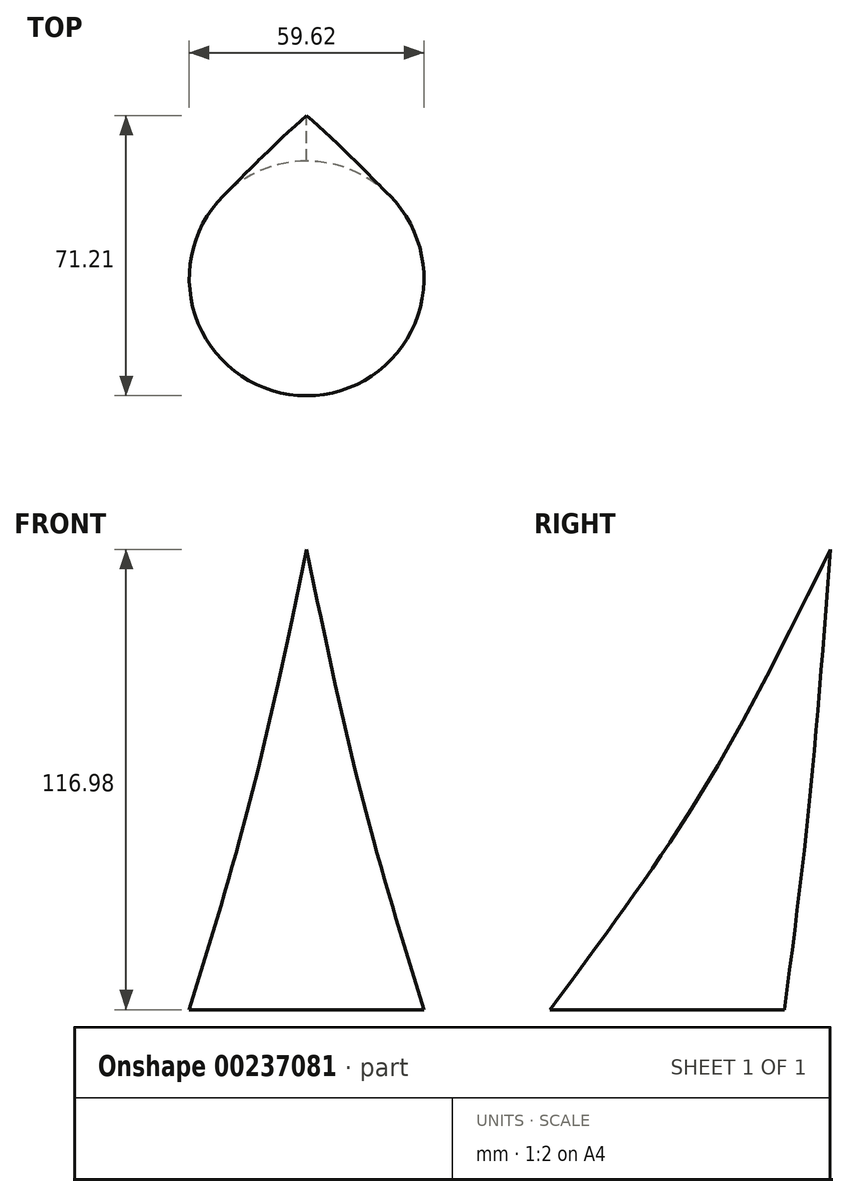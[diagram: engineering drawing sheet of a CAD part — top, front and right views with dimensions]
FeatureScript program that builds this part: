
annotation { "Feature Type Name" : "Feature", "Feature Type Description" : "" }
export const myFeature = defineFeature(function(context is Context, id is Id, definition is map)
    precondition{}
    {
        {
            var Q0;
            Q0=qCreatedBy(makeId("Top.planeOp"),FACE);
            var sketch = newSketch(context, id + "F0", { "sketchPlane" : qUnion([Q0])});
            skCircle(sketch, "E0", {"center": v(0, 0) * mm, "radius": 29.8 * mm});
            skSolve(sketch);
        }
        {
            var Q0;
            Q0=qCreatedBy(makeId("Right.planeOp"),FACE);
            var sketch = newSketch(context, id + "F1", { "sketchPlane" : qUnion([Q0])});
            skArc(sketch, "E1", {"start": v(41.4, 116.98) * mm, "mid": v(10.53, 62.09) * mm, "end": v(0, 0) * mm});
            skSolve(sketch);
        }
        {
            var Q0;
            Q0=qCreatedBy(makeId("Top.planeOp"),FACE);
            cPlane(context, id + "F2", {"entities" : qUnion([Q0]), "cplaneType" : CPlaneType.OFFSET, "offset" : 50 * mm, "width" : 150 * mm, "height" : 150 * mm});
        }
        {
            var Q0;
            Q0=qCreatedBy(id+"F2.planeOp",FACE);
            var sketch = newSketch(context, id + "F3", { "sketchPlane" : qUnion([Q0])});
            skLineSegment(sketch, "E2.0", {"start": v(0, 41.4) * mm, "end": v(0, 0) * mm});
            skCircle(sketch, "E3", {"center": v(0, 20.7) * mm, "radius": 15.15 * mm});
            skSolve(sketch);
        }
        {
            var Q0;
            Q0=makeQuery(id+"F0.imprint","IMPRINT",FACE,{"disambiguationData":[TD([[makeQuery(id+"F0.imprint","IMPRINT",EDGE,{"derivedFrom":sQuery(id+"F0.wireOp",EDGE,"E0")}),1.0]])]});
            var Q1;
            Q1=makeQuery(id+"F3.imprint","IMPRINT",FACE,{"disambiguationData":[TD([[makeQuery(id+"F3.imprint","IMPRINT",EDGE,{"derivedFrom":sQuery(id+"F3.wireOp",EDGE,"E3")}),1.0]])]});
            var Q2;
            Q2=sQuery(id+"F1.wireOp",VERTEX,"E1.start");
            loft(context, id + "F4", {"sheetProfilesArray" : [{ "sheetProfileEntities" : qUnion([Q0]) }, { "sheetProfileEntities" : qUnion([Q1]) }, { "sheetProfileEntities" : qUnion([Q2]) }]});
        }
    });
